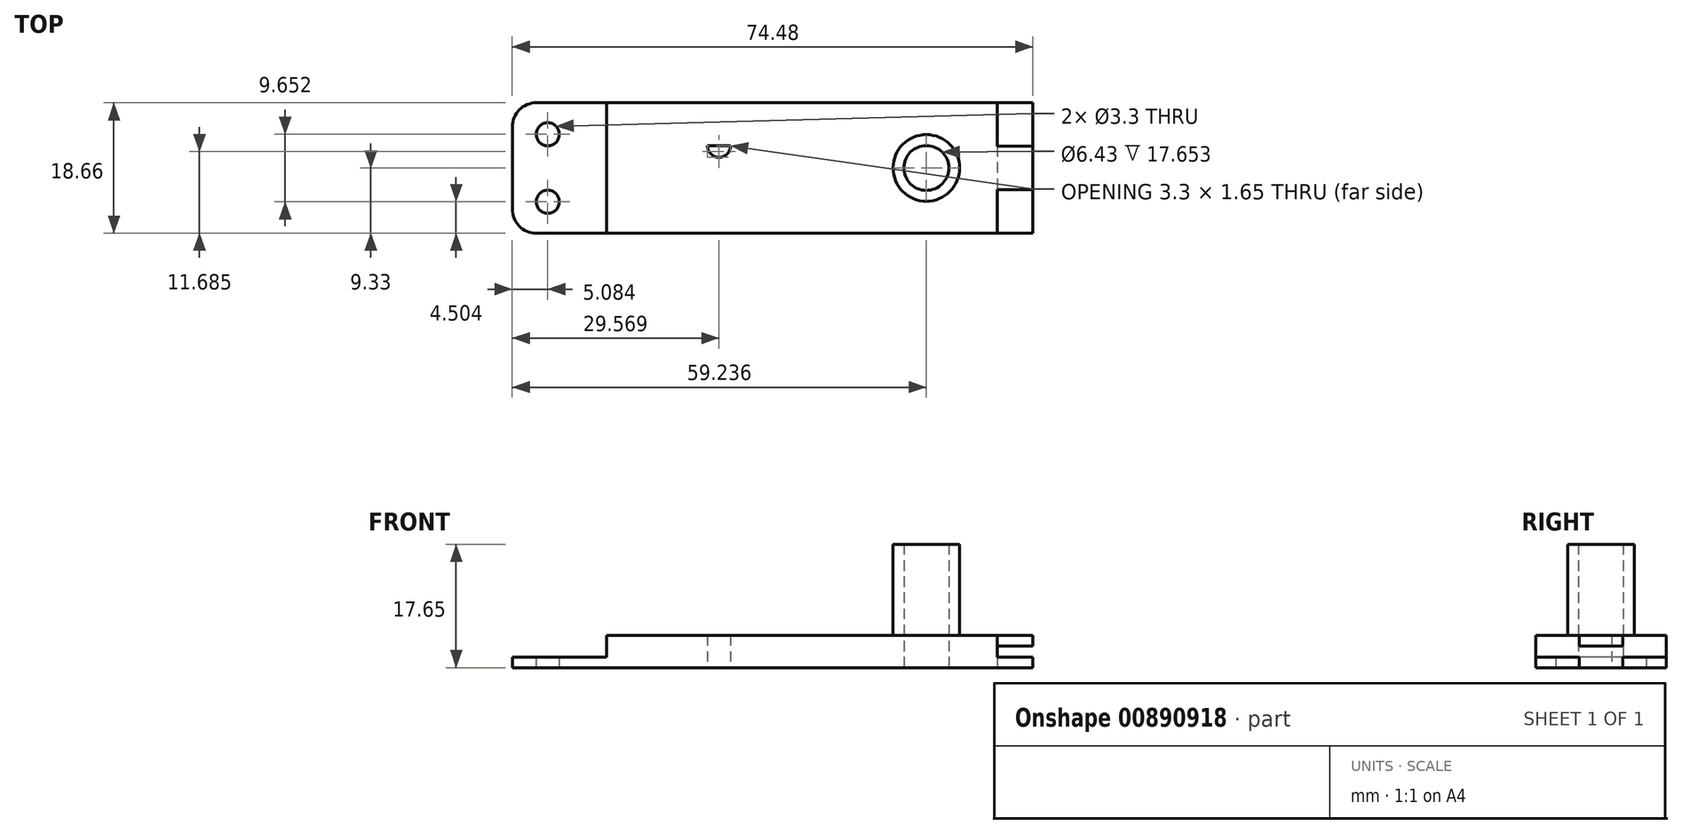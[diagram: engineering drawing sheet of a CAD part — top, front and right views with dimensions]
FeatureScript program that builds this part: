
annotation { "Feature Type Name" : "Feature", "Feature Type Description" : "" }
export const myFeature = defineFeature(function(context is Context, id is Id, definition is map)
    precondition{}
    {
        {
            var Q0;
            Q0=qCreatedBy(makeId("Top.planeOp"),FACE);
            var sketch = newSketch(context, id + "F0", { "sketchPlane" : qUnion([Q0])});
            skLineSegment(sketch, "E0.bottom", {"start": v(37.24, 9.33) * mm, "end": v(-37.24, 9.33) * mm});
            skLineSegment(sketch, "E0.top", {"start": v(37.24, -9.33) * mm, "end": v(-37.24, -9.33) * mm});
            skLineSegment(sketch, "E0.left", {"start": v(37.24, 9.33) * mm, "end": v(37.24, -9.33) * mm});
            skLineSegment(sketch, "E0.right", {"start": v(-37.24, 9.33) * mm, "end": v(-37.24, -9.33) * mm});
            skPoint(sketch, "E0.middle", {"position": v(0, 0) * mm});
            skLineSegment(sketch, "E1", {"start": v(37.24, -9.33) * mm, "end": v(37.24, -3.11) * mm});
            skLineSegment(sketch, "E2", {"start": v(37.24, 9.33) * mm, "end": v(37.24, 3.11) * mm});
            skLineSegment(sketch, "E3", {"start": v(37.24, -9.33) * mm, "end": v(-33.78, -9.33) * mm});
            skLineSegment(sketch, "E4", {"start": v(37.24, 9.33) * mm, "end": v(-33.78, 9.33) * mm});
            skLineSegment(sketch, "E5", {"start": v(-37.24, 9.33) * mm, "end": v(-37.24, 5.88) * mm});
            skLineSegment(sketch, "E6", {"start": v(-37.24, -9.33) * mm, "end": v(-37.24, -5.88) * mm});
            skArc(sketch, "E7", {"start": v(-37.24, -5.88) * mm, "mid": v(-36.22, -8.32) * mm, "end": v(-33.78, -9.33) * mm});
            skArc(sketch, "E8", {"start": v(-33.78, 9.33) * mm, "mid": v(-36.22, 8.32) * mm, "end": v(-37.24, 5.88) * mm});
            skLineSegment(sketch, "E9", {"start": v(-37.24, 3.53) * mm, "end": v(-16.56, 3.53) * mm, "construction": true});
            skLineSegment(sketch, "E10", {"start": v(-16.56, 3.53) * mm, "end": v(-16.56, 9.33) * mm, "construction": true});
            skLineSegment(sketch, "E11", {"start": v(-16.56, 9.33) * mm, "end": v(-16.56, 3.53) * mm, "construction": true});
            skLineSegment(sketch, "E12", {"start": v(-16.56, -9.33) * mm, "end": v(-16.56, 3.53) * mm, "construction": true});
            skLineSegment(sketch, "E13", {"start": v(-16.56, 9.33) * mm, "end": v(-16.56, 3.18) * mm, "construction": true});
            skLineSegment(sketch, "E14", {"start": v(-16.56, -9.33) * mm, "end": v(-16.56, -3.18) * mm, "construction": true});
            skLineSegment(sketch, "E15", {"start": v(-16.56, -3.18) * mm, "end": v(-16.56, 3.18) * mm});
            skLineSegment(sketch, "E16", {"start": v(-16.56, 3.18) * mm, "end": v(1.22, 3.18) * mm});
            skLineSegment(sketch, "E17", {"start": v(-16.56, -3.18) * mm, "end": v(1.22, -3.18) * mm});
            skLineSegment(sketch, "E18", {"start": v(1.22, -3.18) * mm, "end": v(1.22, 3.18) * mm});
            skPoint(sketch, "E19", {"position": v(-7.67, 3.18) * mm});
            skPoint(sketch, "E20", {"position": v(-7.67, -3.18) * mm});
            skLineSegment(sketch, "E21", {"start": v(-7.67, -3.18) * mm, "end": v(-6.02, -3.18) * mm});
            skLineSegment(sketch, "E22", {"start": v(-7.67, 3.18) * mm, "end": v(-6.02, 3.18) * mm});
            skArc(sketch, "E23", {"start": v(-6.02, 3.18) * mm, "mid": v(-7.67, 1.53) * mm, "end": v(-9.32, 3.18) * mm});
            skArc(sketch, "E24", {"start": v(-6.02, -3.18) * mm, "mid": v(-7.67, -1.53) * mm, "end": v(-9.32, -3.18) * mm});
            skLineSegment(sketch, "E25", {"start": v(37.24, 9.33) * mm, "end": v(32.16, 9.33) * mm});
            skLineSegment(sketch, "E26", {"start": v(32.16, 9.33) * mm, "end": v(32.16, -9.33) * mm});
            skLineSegment(sketch, "E27", {"start": v(37.24, -3.11) * mm, "end": v(32.16, -3.11) * mm});
            skLineSegment(sketch, "E28", {"start": v(37.24, 3.11) * mm, "end": v(32.16, 3.11) * mm});
            skLineSegment(sketch, "E29", {"start": v(32.16, 9.33) * mm, "end": v(22, 9.33) * mm, "construction": true});
            skLineSegment(sketch, "E30", {"start": v(22, 9.33) * mm, "end": v(22, -9.33) * mm, "construction": true});
            skPoint(sketch, "E31", {"position": v(22, 0) * mm});
            skCircle(sketch, "E32", {"center": v(22, 0) * mm, "radius": 3.21 * mm});
            skCircle(sketch, "E33", {"center": v(22, 0) * mm, "radius": 4.76 * mm});
            skLineSegment(sketch, "E34", {"start": v(-37.24, 0) * mm, "end": v(-32.16, 0) * mm, "construction": true});
            skLineSegment(sketch, "E35", {"start": v(-32.16, 0) * mm, "end": v(-32.16, 9.33) * mm, "construction": true});
            skLineSegment(sketch, "E36", {"start": v(-32.16, 0) * mm, "end": v(-32.16, -9.33) * mm, "construction": true});
            skLineSegment(sketch, "E37", {"start": v(-32.16, -9.33) * mm, "end": v(-32.16, -4.83) * mm, "construction": true});
            skLineSegment(sketch, "E38", {"start": v(-32.16, 9.33) * mm, "end": v(-32.16, 4.83) * mm, "construction": true});
            skCircle(sketch, "E39", {"center": v(-32.16, 4.83) * mm, "radius": 1.65 * mm});
            skCircle(sketch, "E40", {"center": v(-32.16, -4.83) * mm, "radius": 1.65 * mm});
            skLineSegment(sketch, "E41", {"start": v(-37.24, 0) * mm, "end": v(-23.71, 0) * mm, "construction": true});
            skLineSegment(sketch, "E42", {"start": v(-23.71, 0) * mm, "end": v(-23.71, 9.33) * mm});
            skLineSegment(sketch, "E43", {"start": v(-23.71, 0) * mm, "end": v(-23.71, -9.33) * mm});
            skSolve(sketch);
        }
        {
            var Q0;
            {var subQ0=sQuery(id+"F0.wireOp",EDGE,"E7");Q0=makeQuery(id+"F0.imprint","IMPRINT",FACE,{"disambiguationData":[TD([[makeQuery(id+"F0.imprint","IMPRINT",EDGE,{"derivedFrom":subQ0}),1.0]])]});}
            var Q1;
            {var subQ8=sQuery(id+"F0.wireOp",EDGE,"E15");Q1=makeQuery(id+"F0.imprint","IMPRINT",FACE,{"disambiguationData":[TD([[makeQuery(id+"F0.imprint","IMPRINT",EDGE,{"derivedFrom":subQ8}),1.0]])]});}
            var Q2;
            Q2=makeQuery(id+"F0.imprint","IMPRINT",FACE,{"disambiguationData":[TD([[makeQuery(id+"F0.imprint","IMPRINT",EDGE,{"derivedFrom":sQuery(id+"F0.wireOp",EDGE,"E32")}),-1.0]])]});
            var Q3;
            {var subQ5=sQuery(id+"F0.wireOp",EDGE,"E27");Q3=makeQuery(id+"F0.imprint","IMPRINT",FACE,{"disambiguationData":[TD([[makeQuery(id+"F0.imprint","IMPRINT",EDGE,{"derivedFrom":subQ5}),1.0]])]});}
            var Q4;
            {var subQ5=sQuery(id+"F0.wireOp",EDGE,"E28");Q4=makeQuery(id+"F0.imprint","IMPRINT",FACE,{"disambiguationData":[TD([[makeQuery(id+"F0.imprint","IMPRINT",EDGE,{"derivedFrom":subQ5}),-1.0]])]});}
            var Q5;
            {var subQ0=sQuery(id+"F0.wireOp",EDGE,"E24");Q5=makeQuery(id+"F0.imprint","IMPRINT",FACE,{"disambiguationData":[TD([[makeQuery(id+"F0.imprint","IMPRINT",EDGE,{"derivedFrom":subQ0}),1.0]])]});}
            var Q6;
            {var subQ0=sQuery(id+"F0.wireOp",EDGE,"E23");Q6=makeQuery(id+"F0.imprint","IMPRINT",FACE,{"disambiguationData":[TD([[makeQuery(id+"F0.imprint","IMPRINT",EDGE,{"derivedFrom":subQ0}),-1.0]])]});}
            extrude(context, id + "F1", {"entities" : qUnion([Q0, Q1, Q2, Q3, Q4, Q5, Q6]), "depth" : 1.52 * mm, "offsetDistance" : 25.4 * mm});
        }
        {
            var Q0;
            {var subQ8=sQuery(id+"F0.wireOp",EDGE,"E15");Q0=makeQuery(id+"F0.imprint","IMPRINT",FACE,{"disambiguationData":[TD([[makeQuery(id+"F0.imprint","IMPRINT",EDGE,{"derivedFrom":subQ8}),1.0]])]});}
            var Q1;
            {var subQ0=sQuery(id+"F0.wireOp",EDGE,"E24");Q1=makeQuery(id+"F0.imprint","IMPRINT",FACE,{"disambiguationData":[TD([[makeQuery(id+"F0.imprint","IMPRINT",EDGE,{"derivedFrom":subQ0}),1.0]])]});}
            var Q2;
            {var subQ0=sQuery(id+"F0.wireOp",EDGE,"E23");Q2=makeQuery(id+"F0.imprint","IMPRINT",FACE,{"disambiguationData":[TD([[makeQuery(id+"F0.imprint","IMPRINT",EDGE,{"derivedFrom":subQ0}),-1.0]])]});}
            extrude(context, id + "F2", {"entities" : qUnion([Q0, Q1, Q2]), "operationType" : NewBodyOperationType.ADD, "depth" : 4.65 * mm, "offsetDistance" : 25.4 * mm});
        }
        {
            var Q0;
            {var subQ0=sQuery(id+"F0.wireOp",EDGE,"E27");Q0=makeQuery(id+"F0.imprint","IMPRINT",FACE,{"disambiguationData":[TD([[makeQuery(id+"F0.imprint","IMPRINT",EDGE,{"derivedFrom":subQ0}),-1.0]])]});}
            extrude(context, id + "F3", {"entities" : qUnion([Q0]), "operationType" : NewBodyOperationType.ADD, "depth" : 4.65 * mm, "offsetDistance" : 25.4 * mm, "hasSecondDirection" : true, "secondDirectionOppositeDirection" : false, "secondDirectionDepth" : 3.12 * mm});
        }
        {
            var Q0;
            {var subQ0=sQuery(id+"F0.wireOp",EDGE,"E32");Q0=makeQuery(id+"F2.boolean.opBoolean","SPLIT",FACE,{"disambiguationData":[TD([makeQuery(id+"F1.opExtrude","SWEPT_FACE",FACE,{"disambiguationData":[OSD([subQ0])]})])],"derivedFrom":makeQuery(id+"F1.opExtrude","CAP_FACE",FACE,{"disambiguationData":[OSD([sQuery(id+"F0.wireOp",EDGE,"E0.bottom"),sQuery(id+"F0.wireOp",EDGE,"E0.top"),sQuery(id+"F0.wireOp",EDGE,"E0.left"),sQuery(id+"F0.wireOp",EDGE,"E0.right"),sQuery(id+"F0.wireOp",EDGE,"E7"),sQuery(id+"F0.wireOp",EDGE,"E8"),sQuery(id+"F0.wireOp",EDGE,"E15"),sQuery(id+"F0.wireOp",EDGE,"E16"),sQuery(id+"F0.wireOp",EDGE,"E17"),sQuery(id+"F0.wireOp",EDGE,"E18"),sQuery(id+"F0.wireOp",EDGE,"E23"),sQuery(id+"F0.wireOp",EDGE,"E24"),sQuery(id+"F0.wireOp",EDGE,"E26"),sQuery(id+"F0.wireOp",EDGE,"E27"),sQuery(id+"F0.wireOp",EDGE,"E28"),subQ0,sQuery(id+"F0.wireOp",EDGE,"E39"),sQuery(id+"F0.wireOp",EDGE,"E40")])],"isStart":false})});}
            extrude(context, id + "F4", {"entities" : qUnion([Q0]), "operationType" : NewBodyOperationType.ADD, "depth" : 16.13 * mm, "offsetDistance" : 25.4 * mm});
        }
    });
